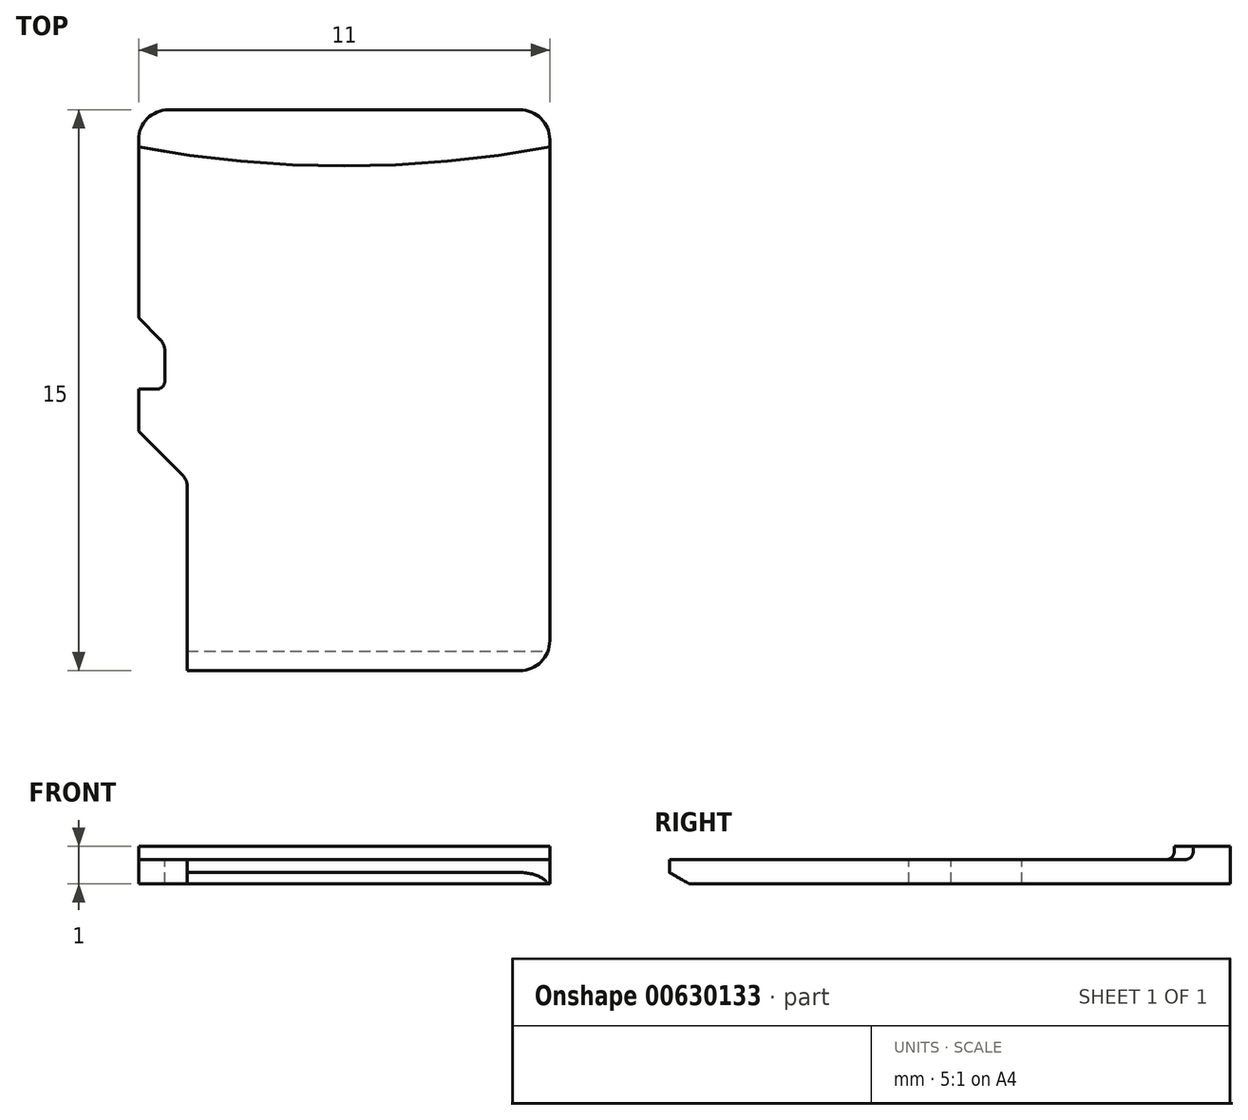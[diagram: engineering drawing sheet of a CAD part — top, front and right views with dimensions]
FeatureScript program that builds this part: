
annotation { "Feature Type Name" : "Feature", "Feature Type Description" : "" }
export const myFeature = defineFeature(function(context is Context, id is Id, definition is map)
    precondition{}
    {
        {
            var Q0;
            Q0=qCreatedBy(makeId("Top.planeOp"),FACE);
            var sketch = newSketch(context, id + "F0", { "sketchPlane" : qUnion([Q0])});
            skLineSegment(sketch, "E0.bottom", {"start": v(0, 0) * mm, "end": v(11, 0) * mm});
            skLineSegment(sketch, "E0.top", {"start": v(0, 15) * mm, "end": v(11, 15) * mm});
            skLineSegment(sketch, "E0.left", {"start": v(0, 0) * mm, "end": v(0, 15) * mm});
            skLineSegment(sketch, "E0.right", {"start": v(11, 0) * mm, "end": v(11, 15) * mm});
            skSolve(sketch);
        }
        {
            var Q0;
            Q0=qSketchRegion(id+"F0",true);
            extrude(context, id + "F1", {"entities" : qUnion([Q0]), "depth" : 1 * mm});
        }
        {
            var Q0;
            Q0=makeQuery(id+"F1.opExtrude","CAP_FACE",FACE,{"disambiguationData":[OSD([sQuery(id+"F0.wireOp",EDGE,"E0.bottom"),sQuery(id+"F0.wireOp",EDGE,"E0.top"),sQuery(id+"F0.wireOp",EDGE,"E0.left"),sQuery(id+"F0.wireOp",EDGE,"E0.right")])],"isStart":false});
            var sketch = newSketch(context, id + "F2", { "sketchPlane" : qUnion([Q0])});
            skLineSegment(sketch, "E1", {"start": v(0, 0) * mm, "end": v(11, 0) * mm});
            skLineSegment(sketch, "E2", {"start": v(11, 0) * mm, "end": v(11, 14) * mm});
            skLineSegment(sketch, "E3", {"start": v(0, 0) * mm, "end": v(0, 14) * mm});
            skArc(sketch, "E4", {"start": v(0, 14) * mm, "mid": v(5.5, 13.5) * mm, "end": v(11, 14) * mm});
            skSolve(sketch);
        }
        {
            var Q0;
            Q0=qSketchRegion(id+"F2",true);
            extrude(context, id + "F3", {"entities" : qUnion([Q0]), "operationType" : NewBodyOperationType.REMOVE, "oppositeDirection" : true, "depth" : 0.35 * mm});
        }
        {
            var Q0;
            Q0=makeQuery(id+"F3.boolean.opBoolean","COPY",FACE,{"derivedFrom":makeQuery(id+"F3.opExtrude","CAP_FACE",FACE,{"disambiguationData":[OSD([sQuery(id+"F2.wireOp",EDGE,"E1"),sQuery(id+"F2.wireOp",EDGE,"E2"),sQuery(id+"F2.wireOp",EDGE,"E3"),sQuery(id+"F2.wireOp",EDGE,"E4")])],"isStart":false})});
            var sketch = newSketch(context, id + "F4", { "sketchPlane" : qUnion([Q0])});
            skLineSegment(sketch, "E5", {"start": v(1.3, 0) * mm, "end": v(1.3, 5.1) * mm});
            skLineSegment(sketch, "E6", {"start": v(1.3, 5.1) * mm, "end": v(0, 6.4) * mm});
            skLineSegment(sketch, "E7", {"start": v(0, 6.4) * mm, "end": v(0, 7.53) * mm});
            skLineSegment(sketch, "E8", {"start": v(0, 7.53) * mm, "end": v(0.7, 7.53) * mm});
            skLineSegment(sketch, "E9", {"start": v(0.7, 7.53) * mm, "end": v(0.7, 8.73) * mm});
            skLineSegment(sketch, "E10", {"start": v(0.7, 8.73) * mm, "end": v(0, 9.43) * mm});
            skLineSegment(sketch, "E11", {"start": v(1.3, 0) * mm, "end": v(0, 0) * mm});
            skLineSegment(sketch, "E12", {"start": v(0, 0) * mm, "end": v(0, 6.4) * mm});
            skLineSegment(sketch, "E13", {"start": v(0, 7.53) * mm, "end": v(0, 9.43) * mm});
            skSolve(sketch);
        }
        {
            var Q0;
            Q0=qSketchRegion(id+"F4",true);
            extrude(context, id + "F5", {"entities" : qUnion([Q0]), "operationType" : NewBodyOperationType.REMOVE, "endBound" : BoundingType.UP_TO_NEXT, "oppositeDirection" : true, "depth" : 25 * mm});
        }
        {
            var Q0;
            Q0=makeQuery(id+"F5.boolean.opBoolean","COPY",EDGE,{"derivedFrom":makeQuery(id+"F5.opExtrude","SWEPT_EDGE",EDGE,{"disambiguationData":[OSD([sQuery(id+"F4.wireOp",EDGE,"E8"),sQuery(id+"F4.wireOp",EDGE,"E9")])]})});
            fillet(context, id + "F6", {"entities" : qUnion([Q0]), "radius" : 0.2 * mm, "tangentPropagation" : true, "allowEdgeOverflow" : false});
        }
        {
            var Q0;
            Q0=makeQuery(id+"F5.boolean.opBoolean","COPY",EDGE,{"derivedFrom":makeQuery(id+"F5.opExtrude","SWEPT_EDGE",EDGE,{"disambiguationData":[OSD([sQuery(id+"F4.wireOp",EDGE,"E9"),sQuery(id+"F4.wireOp",EDGE,"E10")])]})});
            fillet(context, id + "F7", {"entities" : qUnion([Q0]), "radius" : 0.4 * mm, "tangentPropagation" : true, "allowEdgeOverflow" : false});
        }
        {
            var Q0;
            Q0=makeQuery(id+"F3.boolean.opBoolean","COPY",EDGE,{"derivedFrom":makeQuery(id+"F3.opExtrude","CAP_EDGE",EDGE,{"disambiguationData":[OSD([sQuery(id+"F2.wireOp",EDGE,"E4")])],"isStart":false})});
            fillet(context, id + "F8", {"entities" : qUnion([Q0]), "radius" : 0.2 * mm, "tangentPropagation" : true, "allowEdgeOverflow" : false});
        }
        {
            var Q0;
            Q0=makeQuery(id+"F5.boolean.opBoolean","COPY",EDGE,{"derivedFrom":makeQuery(id+"F5.opExtrude","SWEPT_EDGE",EDGE,{"disambiguationData":[OSD([sQuery(id+"F4.wireOp",EDGE,"E5"),sQuery(id+"F4.wireOp",EDGE,"E6")])]})});
            fillet(context, id + "F9", {"entities" : qUnion([Q0]), "radius" : 0.4 * mm, "tangentPropagation" : true, "allowEdgeOverflow" : false});
        }
        {
            var Q0;
            Q0=makeQuery(id+"F1.opExtrude","SWEPT_FACE",FACE,{"disambiguationData":[OSD([sQuery(id+"F0.wireOp",EDGE,"E0.right")])]});
            var sketch = newSketch(context, id + "F10", { "sketchPlane" : qUnion([Q0])});
            skLineSegment(sketch, "E14", {"start": v(0, 0.3) * mm, "end": v(0.52, 0) * mm});
            skLineSegment(sketch, "E15", {"start": v(0, 0.3) * mm, "end": v(0, 0) * mm});
            skLineSegment(sketch, "E16", {"start": v(0, 0) * mm, "end": v(0.52, 0) * mm});
            skSolve(sketch);
        }
        {
            var Q0;
            Q0=qSketchRegion(id+"F10",true);
            extrude(context, id + "F11", {"entities" : qUnion([Q0]), "operationType" : NewBodyOperationType.REMOVE, "endBound" : BoundingType.UP_TO_NEXT, "oppositeDirection" : true, "depth" : 25 * mm});
        }
        {
            var Q0;
            Q0=makeQuery(id+"F1.opExtrude","SWEPT_EDGE",EDGE,{"disambiguationData":[OSD([sQuery(id+"F0.wireOp",EDGE,"E0.bottom"),sQuery(id+"F0.wireOp",EDGE,"E0.right")])]});
            var Q1;
            Q1=makeQuery(id+"F5.boolean.opBoolean","COPY",EDGE,{"derivedFrom":makeQuery(id+"F5.opExtrude","SWEPT_EDGE",EDGE,{"disambiguationData":[OSD([sQuery(id+"F2.wireOp",EDGE,"E1"),sQuery(id+"F4.wireOp",EDGE,"E5"),sQuery(id+"F4.wireOp",EDGE,"E11")])]})});
            var Q2;
            Q2=makeQuery(id+"F1.opExtrude","SWEPT_EDGE",EDGE,{"disambiguationData":[OSD([sQuery(id+"F0.wireOp",EDGE,"E0.top"),sQuery(id+"F0.wireOp",EDGE,"E0.left")])]});
            var Q3;
            Q3=makeQuery(id+"F1.opExtrude","SWEPT_EDGE",EDGE,{"disambiguationData":[OSD([sQuery(id+"F0.wireOp",EDGE,"E0.top"),sQuery(id+"F0.wireOp",EDGE,"E0.right")])]});
            fillet(context, id + "F12", {"entities" : qUnion([Q0, Q1, Q2, Q3]), "radius" : 0.8 * mm, "tangentPropagation" : true, "allowEdgeOverflow" : false});
        }
    });
